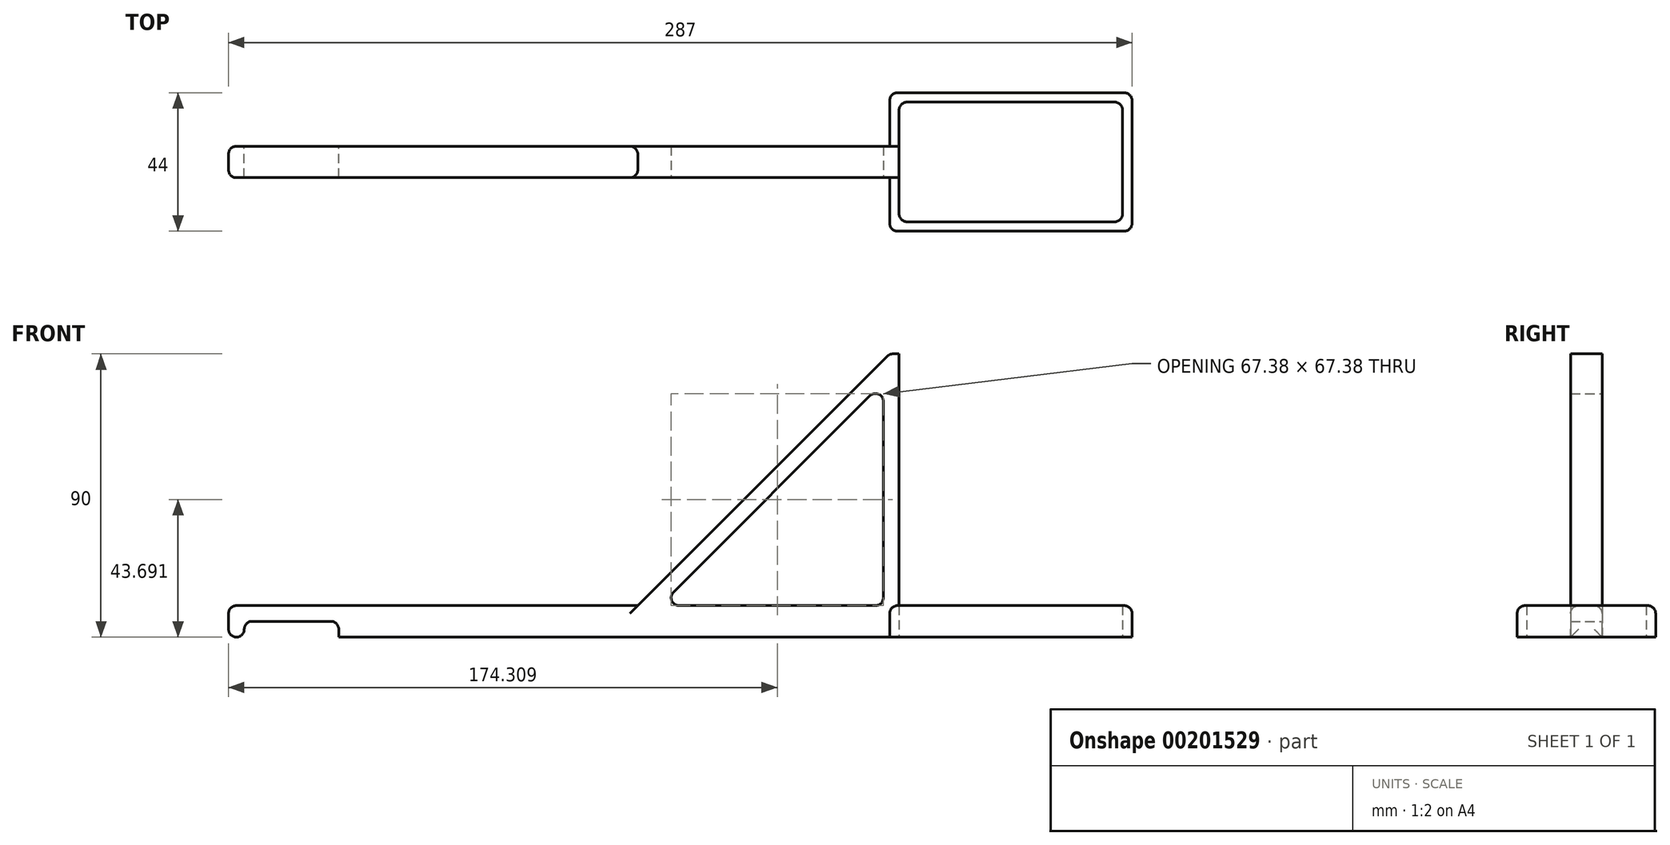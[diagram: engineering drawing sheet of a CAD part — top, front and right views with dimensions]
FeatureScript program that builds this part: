
annotation { "Feature Type Name" : "Feature", "Feature Type Description" : "" }
export const myFeature = defineFeature(function(context is Context, id is Id, definition is map)
    precondition{}
    {
        {
            var Q0;
            Q0=qCreatedBy(makeId("Top.planeOp"),FACE);
            var sketch = newSketch(context, id + "F7", { "sketchPlane" : qUnion([Q0])});
            skLineSegment(sketch, "E0.bottom", {"start": v(35.5, -19) * mm, "end": v(-35.5, -19) * mm});
            skLineSegment(sketch, "E0.top", {"start": v(35.5, 19) * mm, "end": v(-35.5, 19) * mm});
            skLineSegment(sketch, "E0.left", {"start": v(35.5, -19) * mm, "end": v(35.5, 19) * mm});
            skLineSegment(sketch, "E0.right", {"start": v(-35.5, -19) * mm, "end": v(-35.5, 19) * mm});
            skPoint(sketch, "E0.middle", {"position": v(0, 0) * mm});
            skLineSegment(sketch, "E1.bottom", {"start": v(38.5, -22) * mm, "end": v(-38.5, -22) * mm});
            skLineSegment(sketch, "E1.top", {"start": v(38.5, 22) * mm, "end": v(-38.5, 22) * mm});
            skLineSegment(sketch, "E1.left", {"start": v(38.5, -22) * mm, "end": v(38.5, 22) * mm});
            skLineSegment(sketch, "E1.right", {"start": v(-38.5, -22) * mm, "end": v(-38.5, 22) * mm});
            skLineSegment(sketch, "E2", {"start": v(32.9, -19) * mm, "end": v(32.9, -22) * mm, "construction": true});
            skLineSegment(sketch, "E3", {"start": v(35.5, -17) * mm, "end": v(38.5, -17) * mm, "construction": true});
            skLineSegment(sketch, "E4.bottom", {"start": v(-38.5, -5) * mm, "end": v(-248.5, -5) * mm});
            skLineSegment(sketch, "E4.top", {"start": v(-38.5, 5) * mm, "end": v(-248.5, 5) * mm});
            skLineSegment(sketch, "E4.left", {"start": v(-38.5, -5) * mm, "end": v(-38.5, 5) * mm});
            skLineSegment(sketch, "E4.right", {"start": v(-248.5, -5) * mm, "end": v(-248.5, 5) * mm});
            skLineSegment(sketch, "E5", {"start": v(-43.46, 5) * mm, "end": v(-43.46, 22) * mm, "construction": true});
            skLineSegment(sketch, "E6", {"start": v(-43.46, -5) * mm, "end": v(-43.46, -22) * mm, "construction": true});
            skSolve(sketch);
        }
        {
            var Q0;
            Q0=makeQuery(id+"F7.imprint","IMPRINT",FACE,{"disambiguationData":[TD([[makeQuery(id+"F7.imprint","IMPRINT",EDGE,{"derivedFrom":sQuery(id+"F7.wireOp",EDGE,"E0.bottom")}),1.0]])]});
            var Q1;
            Q1=makeQuery(id+"F7.imprint","IMPRINT",FACE,{"disambiguationData":[TD([[makeQuery(id+"F7.imprint","IMPRINT",EDGE,{"derivedFrom":sQuery(id+"F7.wireOp",EDGE,"E4.bottom")}),-1.0]])]});
            extrude(context, id + "F0", {"entities" : qUnion([Q0, Q1]), "depth" : 10 * mm});
        }
        {
            var Q0;
            Q0=makeQuery(id+"F0.opExtrude","SWEPT_FACE",FACE,{"disambiguationData":[OSD([sQuery(id+"F7.wireOp",EDGE,"E4.bottom")])]});
            var sketch = newSketch(context, id + "F1", { "sketchPlane" : qUnion([Q0])});
            skLineSegment(sketch, "E7", {"start": v(-38.5, 10) * mm, "end": v(-38.5, 90) * mm});
            skLineSegment(sketch, "E8", {"start": v(-38.5, 90) * mm, "end": v(-118.5, 10) * mm});
            skLineSegment(sketch, "E9", {"start": v(-40.5, 10) * mm, "end": v(-40.5, 80.93) * mm});
            skLineSegment(sketch, "E10", {"start": v(-40.5, 80.93) * mm, "end": v(-111.43, 10) * mm});
            skSolve(sketch);
        }
        {
            var Q0;
            {var subQ5=sQuery(id+"F1.wireOp",EDGE,"E7");Q0=makeQuery(id+"F1.imprint","IMPRINT",FACE,{"disambiguationData":[TD([[makeQuery(id+"F1.imprint","IMPRINT",EDGE,{"derivedFrom":subQ5}),1.0]])]});}
            extrude(context, id + "F2", {"entities" : qUnion([Q0]), "operationType" : NewBodyOperationType.ADD, "oppositeDirection" : true, "depth" : 10 * mm});
        }
        {
            var Q0;
            Q0=makeQuery(id+"F2.opExtrude","SWEPT_FACE",FACE,{"disambiguationData":[OSD([sQuery(id+"F1.wireOp",EDGE,"E7")])]});
            extrude(context, id + "F3", {"entities" : qUnion([Q0]), "operationType" : NewBodyOperationType.ADD, "depth" : 3 * mm});
        }
        {
            var Q0;
            Q0=makeQuery(id+"F0.opExtrude","CAP_FACE",FACE,{"disambiguationData":[OSD([sQuery(id+"F7.wireOp",EDGE,"E0.bottom"),sQuery(id+"F7.wireOp",EDGE,"E0.top"),sQuery(id+"F7.wireOp",EDGE,"E0.left"),sQuery(id+"F7.wireOp",EDGE,"E0.right"),sQuery(id+"F7.wireOp",EDGE,"E1.bottom"),sQuery(id+"F7.wireOp",EDGE,"E1.top"),sQuery(id+"F7.wireOp",EDGE,"E1.left"),sQuery(id+"F7.wireOp",EDGE,"E1.right"),sQuery(id+"F7.wireOp",EDGE,"E4.bottom"),sQuery(id+"F7.wireOp",EDGE,"E4.top"),sQuery(id+"F7.wireOp",EDGE,"E4.right")])],"isStart":true});
            var sketch = newSketch(context, id + "F4", { "sketchPlane" : qUnion([Q0])});
            skLineSegment(sketch, "E11.bottom", {"start": v(-243.5, 5) * mm, "end": v(-213.5, 5) * mm});
            skLineSegment(sketch, "E11.top", {"start": v(-243.5, -5) * mm, "end": v(-213.5, -5) * mm});
            skLineSegment(sketch, "E11.left", {"start": v(-243.5, 5) * mm, "end": v(-243.5, -5) * mm});
            skLineSegment(sketch, "E11.right", {"start": v(-213.5, 5) * mm, "end": v(-213.5, -5) * mm});
            skSolve(sketch);
        }
        {
            var Q0;
            Q0=makeQuery(id+"F4.imprint","IMPRINT",FACE,{"disambiguationData":[TD([[makeQuery(id+"F4.imprint","IMPRINT",EDGE,{"derivedFrom":sQuery(id+"F4.wireOp",EDGE,"E11.bottom")}),1.0]])]});
            extrude(context, id + "F5", {"entities" : qUnion([Q0]), "operationType" : NewBodyOperationType.REMOVE, "oppositeDirection" : true, "depth" : 5 * mm});
        }
        {
            var Q0;
            Q0=makeQuery(id+"F5.boolean.opBoolean","COPY",EDGE,{"derivedFrom":makeQuery(id+"F5.opExtrude","CAP_EDGE",EDGE,{"disambiguationData":[OSD([sQuery(id+"F4.wireOp",EDGE,"E11.right")])],"isStart":false})});
            var Q1;
            Q1=makeQuery(id+"F5.boolean.opBoolean","COPY",EDGE,{"derivedFrom":makeQuery(id+"F5.opExtrude","CAP_EDGE",EDGE,{"disambiguationData":[OSD([sQuery(id+"F4.wireOp",EDGE,"E11.right")])],"isStart":true})});
            var Q2;
            Q2=makeQuery(id+"F5.boolean.opBoolean","COPY",EDGE,{"derivedFrom":makeQuery(id+"F5.opExtrude","CAP_EDGE",EDGE,{"disambiguationData":[OSD([sQuery(id+"F4.wireOp",EDGE,"E11.left")])],"isStart":true})});
            var Q3;
            Q3=makeQuery(id+"F5.boolean.opBoolean","COPY",EDGE,{"derivedFrom":makeQuery(id+"F5.opExtrude","CAP_EDGE",EDGE,{"disambiguationData":[OSD([sQuery(id+"F4.wireOp",EDGE,"E11.left")])],"isStart":false})});
            var Q4;
            Q4=makeQuery(id+"F0.opExtrude","CAP_EDGE",EDGE,{"disambiguationData":[OSD([sQuery(id+"F7.wireOp",EDGE,"E4.right")])],"isStart":false});
            var Q5;
            Q5=makeQuery(id+"F0.opExtrude","CAP_EDGE",EDGE,{"disambiguationData":[OSD([sQuery(id+"F7.wireOp",EDGE,"E4.right")])],"isStart":true});
            var Q6;
            Q6=makeQuery(id+"F2.opExtrude","SWEPT_EDGE",EDGE,{"disambiguationData":[OSD([sQuery(id+"F7.wireOp",EDGE,"E4.bottom"),sQuery(id+"F1.wireOp",EDGE,"E8")])]});
            var Q7;
            {var subQ0=sQuery(id+"F1.wireOp",EDGE,"E8");var subQ1=sQuery(id+"F1.wireOp",EDGE,"E7");Q7=makeQuery(id+"F3.boolean.opBoolean","MERGE",EDGE,{"derivedFrom":[makeQuery(id+"F2.opExtrude","SWEPT_EDGE",EDGE,{"disambiguationData":[OSD([subQ1,subQ0])]}),makeQuery(id+"F3.opExtrude","CAP_EDGE",EDGE,{"disambiguationData":[OSD([subQ1,subQ0])],"isStart":true})]});}
            var Q8;
            Q8=makeQuery(id+"F2.opExtrude","SWEPT_EDGE",EDGE,{"disambiguationData":[OSD([sQuery(id+"F7.wireOp",EDGE,"E4.bottom"),sQuery(id+"F1.wireOp",EDGE,"E9")])]});
            var Q9;
            Q9=makeQuery(id+"F2.opExtrude","SWEPT_EDGE",EDGE,{"disambiguationData":[OSD([sQuery(id+"F1.wireOp",EDGE,"E9"),sQuery(id+"F1.wireOp",EDGE,"E10")])]});
            var Q10;
            Q10=makeQuery(id+"F2.opExtrude","SWEPT_EDGE",EDGE,{"disambiguationData":[OSD([sQuery(id+"F7.wireOp",EDGE,"E4.bottom"),sQuery(id+"F1.wireOp",EDGE,"E10")])]});
            var Q11;
            Q11=makeQuery(id+"F0.opExtrude","SWEPT_EDGE",EDGE,{"disambiguationData":[OSD([sQuery(id+"F7.wireOp",EDGE,"E0.top"),sQuery(id+"F7.wireOp",EDGE,"E0.right")])]});
            var Q12;
            Q12=makeQuery(id+"F0.opExtrude","SWEPT_EDGE",EDGE,{"disambiguationData":[OSD([sQuery(id+"F7.wireOp",EDGE,"E0.bottom"),sQuery(id+"F7.wireOp",EDGE,"E0.right")])]});
            var Q13;
            Q13=makeQuery(id+"F0.opExtrude","SWEPT_EDGE",EDGE,{"disambiguationData":[OSD([sQuery(id+"F7.wireOp",EDGE,"E1.bottom"),sQuery(id+"F7.wireOp",EDGE,"E1.right")])]});
            var Q14;
            Q14=makeQuery(id+"F0.opExtrude","SWEPT_EDGE",EDGE,{"disambiguationData":[OSD([sQuery(id+"F7.wireOp",EDGE,"E1.top"),sQuery(id+"F7.wireOp",EDGE,"E1.right")])]});
            var Q15;
            Q15=makeQuery(id+"F0.opExtrude","SWEPT_EDGE",EDGE,{"disambiguationData":[OSD([sQuery(id+"F7.wireOp",EDGE,"E0.bottom"),sQuery(id+"F7.wireOp",EDGE,"E0.left")])]});
            var Q16;
            Q16=makeQuery(id+"F0.opExtrude","SWEPT_EDGE",EDGE,{"disambiguationData":[OSD([sQuery(id+"F7.wireOp",EDGE,"E0.top"),sQuery(id+"F7.wireOp",EDGE,"E0.left")])]});
            var Q17;
            Q17=makeQuery(id+"F0.opExtrude","SWEPT_EDGE",EDGE,{"disambiguationData":[OSD([sQuery(id+"F7.wireOp",EDGE,"E1.top"),sQuery(id+"F7.wireOp",EDGE,"E1.left")])]});
            var Q18;
            Q18=makeQuery(id+"F0.opExtrude","SWEPT_EDGE",EDGE,{"disambiguationData":[OSD([sQuery(id+"F7.wireOp",EDGE,"E1.bottom"),sQuery(id+"F7.wireOp",EDGE,"E1.left")])]});
            var Q19;
            Q19=makeQuery(id+"F3.opExtrude","SWEPT_EDGE",EDGE,{"disambiguationData":[OSD([sQuery(id+"F7.wireOp",EDGE,"E1.right"),sQuery(id+"F7.wireOp",EDGE,"E4.bottom"),sQuery(id+"F7.wireOp",EDGE,"E4.left"),sQuery(id+"F1.wireOp",EDGE,"E7")])]});
            var Q20;
            Q20=makeQuery(id+"F3.opExtrude","SWEPT_EDGE",EDGE,{"disambiguationData":[OSD([sQuery(id+"F7.wireOp",EDGE,"E1.right"),sQuery(id+"F7.wireOp",EDGE,"E4.bottom"),sQuery(id+"F7.wireOp",EDGE,"E4.top"),sQuery(id+"F7.wireOp",EDGE,"E4.left"),sQuery(id+"F1.wireOp",EDGE,"E7")])]});
            var Q21;
            {var subQ1=sQuery(id+"F7.wireOp",EDGE,"E4.bottom");var subQ2=sQuery(id+"F7.wireOp",EDGE,"E4.right");Q21=makeQuery(id+"F2.boolean.opBoolean","SPLIT",EDGE,{"disambiguationData":[TD([makeQuery(id+"F0.opExtrude","SWEPT_FACE",FACE,{"disambiguationData":[OSD([subQ2])]})])],"derivedFrom":makeQuery(id+"F0.opExtrude","CAP_EDGE",EDGE,{"disambiguationData":[OSD([subQ1])],"isStart":false})});}
            var Q22;
            {var subQ2=sQuery(id+"F7.wireOp",EDGE,"E4.right");var subQ3=sQuery(id+"F7.wireOp",EDGE,"E4.top");Q22=makeQuery(id+"F2.boolean.opBoolean","SPLIT",EDGE,{"disambiguationData":[TD([makeQuery(id+"F0.opExtrude","SWEPT_FACE",FACE,{"disambiguationData":[OSD([subQ2])]})])],"derivedFrom":makeQuery(id+"F0.opExtrude","CAP_EDGE",EDGE,{"disambiguationData":[OSD([subQ3])],"isStart":false})});}
            var Q23;
            Q23=makeQuery(id+"F0.opExtrude","CAP_EDGE",EDGE,{"disambiguationData":[OSD([sQuery(id+"F7.wireOp",EDGE,"E1.bottom")])],"isStart":false});
            var Q24;
            {var subQ0=sQuery(id+"F7.wireOp",EDGE,"E1.right");Q24=makeQuery(id+"F0.opExtrude","CAP_EDGE",EDGE,{"disambiguationData":[OSD([subQ0]),TDD([makeQuery(id+"F7.imprint","IMPRINT",EDGE,{"disambiguationData":[TD([[makeQuery(id+"F7.imprint","INTERSECT",VERTEX,{"derivedFrom":[sQuery(id+"F7.wireOp",EDGE,"E1.bottom"),subQ0]}),-1.0]])],"derivedFrom":subQ0})])],"isStart":false});}
            var Q25;
            Q25=makeQuery(id+"F0.opExtrude","CAP_EDGE",EDGE,{"disambiguationData":[OSD([sQuery(id+"F7.wireOp",EDGE,"E1.left")])],"isStart":false});
            var Q26;
            Q26=makeQuery(id+"F0.opExtrude","CAP_EDGE",EDGE,{"disambiguationData":[OSD([sQuery(id+"F7.wireOp",EDGE,"E1.top")])],"isStart":false});
            var Q27;
            {var subQ0=sQuery(id+"F7.wireOp",EDGE,"E1.right");Q27=makeQuery(id+"F0.opExtrude","CAP_EDGE",EDGE,{"disambiguationData":[OSD([subQ0]),TDD([makeQuery(id+"F7.imprint","IMPRINT",EDGE,{"disambiguationData":[TD([[makeQuery(id+"F7.imprint","INTERSECT",VERTEX,{"derivedFrom":[sQuery(id+"F7.wireOp",EDGE,"E1.top"),subQ0]}),1.0]])],"derivedFrom":subQ0})])],"isStart":false});}
            var Q28;
            Q28=makeQuery(id+"F0.opExtrude","SWEPT_EDGE",EDGE,{"disambiguationData":[OSD([sQuery(id+"F7.wireOp",EDGE,"E4.top"),sQuery(id+"F7.wireOp",EDGE,"E4.right")])]});
            var Q29;
            Q29=makeQuery(id+"F0.opExtrude","SWEPT_EDGE",EDGE,{"disambiguationData":[OSD([sQuery(id+"F7.wireOp",EDGE,"E4.bottom"),sQuery(id+"F7.wireOp",EDGE,"E4.right")])]});
            var Q30;
            Q30=makeQuery(id+"F5.boolean.opBoolean","COPY",EDGE,{"derivedFrom":makeQuery(id+"F5.opExtrude","SWEPT_EDGE",EDGE,{"disambiguationData":[OSD([sQuery(id+"F7.wireOp",EDGE,"E4.top"),sQuery(id+"F4.wireOp",EDGE,"E11.top"),sQuery(id+"F4.wireOp",EDGE,"E11.right")])]})});
            var Q31;
            Q31=makeQuery(id+"F5.boolean.opBoolean","COPY",EDGE,{"derivedFrom":makeQuery(id+"F5.opExtrude","CAP_EDGE",EDGE,{"disambiguationData":[OSD([sQuery(id+"F4.wireOp",EDGE,"E11.bottom")])],"isStart":false})});
            fillet(context, id + "F6", {"entities" : qUnion([Q0, Q1, Q2, Q3, Q4, Q5, Q6, Q7, Q8, Q9, Q10, Q11, Q12, Q13, Q14, Q15, Q16, Q17, Q18, Q19, Q20, Q21, Q22, Q23, Q24, Q25, Q26, Q27, Q28, Q29, Q30, Q31]), "radius" : 2.5 * mm, "tangentPropagation" : true, "allowEdgeOverflow" : false});
        }
    });
